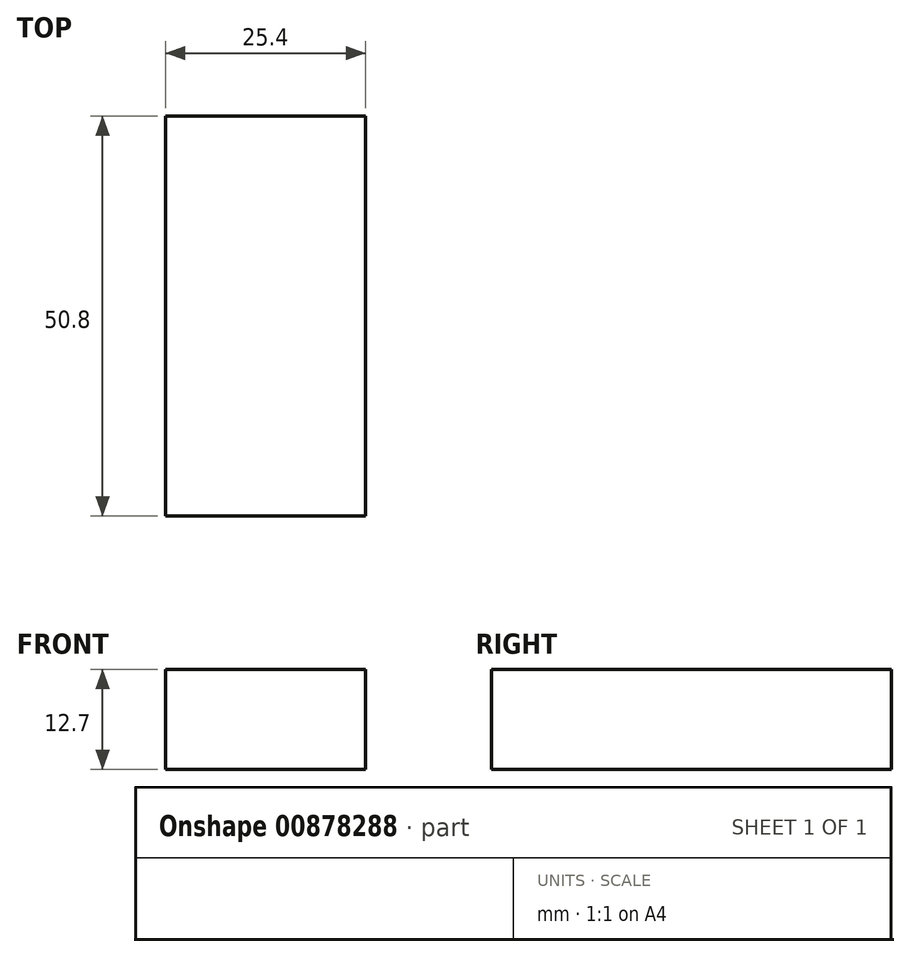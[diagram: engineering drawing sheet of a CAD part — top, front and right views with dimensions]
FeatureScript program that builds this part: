
annotation { "Feature Type Name" : "Feature", "Feature Type Description" : "" }
export const myFeature = defineFeature(function(context is Context, id is Id, definition is map)
    precondition{}
    {
        {
            var Q0;
            Q0=qCreatedBy(makeId("Top.planeOp"),FACE);
            var sketch = newSketch(context, id + "F0", { "sketchPlane" : qUnion([Q0])});
            skLineSegment(sketch, "E0.bottom", {"start": v(0, 0) * mm, "end": v(25.4, 0) * mm});
            skLineSegment(sketch, "E0.top", {"start": v(0, 50.8) * mm, "end": v(25.4, 50.8) * mm});
            skLineSegment(sketch, "E0.left", {"start": v(0, 0) * mm, "end": v(0, 50.8) * mm});
            skLineSegment(sketch, "E0.right", {"start": v(25.4, 0) * mm, "end": v(25.4, 50.8) * mm});
            skSolve(sketch);
        }
        {
            var Q0;
            Q0=makeQuery(id+"F0.imprint","IMPRINT",FACE,{"disambiguationData":[TD([[makeQuery(id+"F0.imprint","IMPRINT",EDGE,{"derivedFrom":sQuery(id+"F0.wireOp",EDGE,"E0.bottom")}),1.0]])]});
            extrude(context, id + "F1", {"entities" : qUnion([Q0]), "depth" : 12.7 * mm, "offsetDistance" : 25 * mm});
        }
    });
